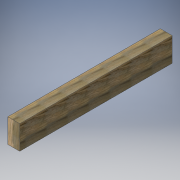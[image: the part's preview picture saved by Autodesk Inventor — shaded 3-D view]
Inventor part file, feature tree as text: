
AUTODESK INVENTOR PART (.ipt)
format: ipt  version: 2016 (Build 200138000, 138)  size: 107,520 bytes
history: native  units: in
note: dims shown in document units (in); Inventor stores cm internally (conversion verified against a paired STEP export)
features: extrude x1, sketch x1
ambient origin geometry x8: Origin, YZ Plane, XZ Plane, XY Plane, X Axis, Y Axis, Z Axis, Center Point
bodies: Solid1 (feature_tree)
feature tree (2):
  extrude  "Extrusion1"  Depth=4.0in
  sketch  "Sketch1"  dims[d0=2.0in d1=4.0in d2=25.5in d3=0.0in]
